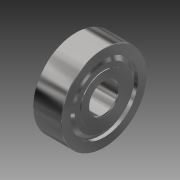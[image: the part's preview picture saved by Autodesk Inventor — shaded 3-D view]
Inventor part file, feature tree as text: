
AUTODESK INVENTOR PART (.ipt)
format: ipt  version: 2014 (Build 180170000, 170)  size: 480,768 bytes
history: native  units: in
note: dims shown in document units (in); Inventor stores cm internally (conversion verified against a paired STEP export)
features: other x11, imported_body x10, extrude x1, fillet x1, sketch x1
ambient origin geometry x8: Origin, YZ Plane, XZ Plane, XY Plane, X Axis, Y Axis, Z Axis, Center Point
bodies: Body1 (feature_tree), Body2 (feature_tree), Body3 (feature_tree), Body4 (feature_tree), Body5 (feature_tree), Body6 (feature_tree), Body7 (feature_tree), Body8 (feature_tree), Body9 (feature_tree), Body10 (feature_tree)
feature tree (24):
  other  "1614ZZ"
  other  "1614ZZ1"
  extrude  "Extrusion1"  Depth=0.01in
  fillet  "Fillet1"  [1 undecoded]
  other  "1614ZZ_1"
  other  "1614ZZ_2"
  other  "1614ZZ_3"
  other  "1614ZZ_4"
  other  "1614ZZ_5"
  other  "1614ZZ_6"
  other  "1614ZZ_7"
  other  "1614ZZ_8"
  other  "1614ZZ_9"
  imported_body  "Base1"
  imported_body  "Base2"
  imported_body  "Base3"
  imported_body  "Base4"
  imported_body  "Base5"
  imported_body  "Base6"
  imported_body  "Base7"
  imported_body  "Base8"
  imported_body  "Base9"
  imported_body  "Base10"
  sketch  "Sketch1"  dims[d0=1.0in d1=0.0in d2=0.01in]
note: 1 required parameter value undecoded (feature->parameter linkage not recoverable at this tier; creation-order binding heuristic only, values carry confidence <= 0.55)
